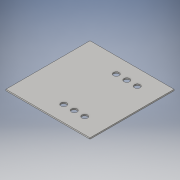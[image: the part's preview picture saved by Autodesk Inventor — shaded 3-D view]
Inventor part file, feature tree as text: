
AUTODESK INVENTOR PART (.ipt)
format: ipt  version: 2016 (Build 200138000, 138)  size: 106,496 bytes
history: native  units: in
note: dims shown in document units (in); Inventor stores cm internally (conversion verified against a paired STEP export)
features: extrude x1, sketch x1
ambient origin geometry x8: Origin, YZ Plane, XZ Plane, XY Plane, X Axis, Y Axis, Z Axis, Center Point
bodies: Solid1 (feature_tree)
feature tree (2):
  extrude  "Extrusion1"  Depth=4.0in
  sketch  "Sketch1"  dims[d0=4.0in d1=4.0in d3=0.27in d4=0.5in d5=0.5in d6=1.0in d8=0.75in d9=0.75in d10=0.27in d11=0.5in d12=0.5in d13=0.0625in d14=0.0in]
